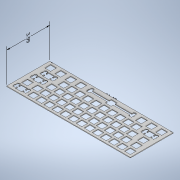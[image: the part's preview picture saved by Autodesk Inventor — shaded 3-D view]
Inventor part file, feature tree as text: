
AUTODESK INVENTOR PART (.ipt)
format: ipt  version: 2022 (Build 260153000, 153)  size: 581,632 bytes
history: native  units: in
note: dims shown in document units (in); Inventor stores cm internally (conversion verified against a paired STEP export)
features: other x3, extrude x1, sketch x1
ambient origin geometry x8: Origin, YZ Plane, XZ Plane, XY Plane, X Axis, Y Axis, Z Axis, Center Point
bodies: Solid1 (feature_tree)
feature tree (5):
  other  "Annotations"
  extrude  "Extrusion1"  Depth=11.4862in TaperAngle=0.0deg
  sketch  "Sketch1"  dims[d0=0.0591in d1=0.0in d2=11.4862in d3=0.0in d4=0.3937in d5=3.9862in]
  other  "Linear Dimension 1"
  other  "Linear Dimension 2"
